# Revit family: Gleitschlitten Typ HV1, m.D., Ø500 bis Ø508mm, h=100mm bis h=155mm
name_source: partatom
category: HLS-Bauteile
revit_build: Autodesk Revit 2018 (Build: 20190510_1515(x64)
units: mm (PartAtom-declared; Revit-internal decimal feet)

## family parameters
Arbeitsebenenbasiert = Ja
Beim Laden mit Abzugskörper schneiden = Nein
Bemaßung runder Anschluss = Durchmesser verwenden
Gemeinsam genutzt = Ja
Immer vertikal = Nein
Klassifizierung = Keine
Raumberechnungspunkt = Nein
Teiletyp = Normal

## types (2) — shared parameters
A (Breite) = 254 mm  [stored 0.833333 ft]
Baustoffklasse = B2
Breite Schellenband = 50 mm
Breite Unterbau = 370 mm
Dämmstärke = 6 mm  [stored 0.019685 ft]
Fabrikat = MEFA
Kurztext1 = Gleitschlitten A HV 100-150 50x5
L = 280 mm  [stored 0.918635 ft]
Länge Unterbau = 390 mm
Mengeneinheit = St
Schalldämmeinlage = Gummi EPDM
Schuh = TL-Fuß für Gleitschl.2Lo.14 : 9000818
Sicherheitsfaktor = 1.54
Stärke Material = 8 mm  [stored 0.0262467 ft]
Stärke Schellenband = 5 mm
Verschluss = Mutter / Verschluss-Schraube
Verschluss-Schraube = M12
Vorgabe-Ansicht = 1219 mm
max. Höhe Unterbau = 150 mm
max. Temperaturbeständigkeit = 100 °C
min. Höhe Unterbau = 100 mm
vpe = 1

## per-type parameters (varying)
| type | Artikelnummer | EAN | Flachmaterial | Gewicht | Gewicht pro Bauteil | Kurztext2 | Rohraußendurchmesser | Schellenteil |
| Gleitschlitten HV1, m.D., Ø500mm, h=100mm bis h=155mm | 142afb0500 | 4250928462961 | Flachmaterial nach DIN (50-5 und 70-8) für HV1 : für Ø500 | 26.17 kg | 26.17 kg | 500 mm EPDM fsv | 500 mm  [stored 1.64042 ft] | Schellenteil für HV mit RS m.D : Schelleteil für 500 m.D. |
| Gleitschlitten HV1, m.D., Ø508mm, h=100mm bis h=155mm | 142afb0508 | 4250928462978 | Flachmaterial nach DIN (50-5 und 70-8) für HV1 : für Ø508 | 26.29 kg | 26.29 kg | 508 mm EPDM fsv | 508 mm | Schellenteil für HV mit RS m.D : Schelleteil für 508 m.D. |

note: [stored X ft] marks values corroborated as IEEE doubles in the binary element streams (Revit-internal decimal feet)

## geometry (parser evidence)
native form markers: Sweep x17
no freeform markers — native parametric forms only
